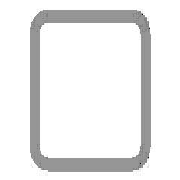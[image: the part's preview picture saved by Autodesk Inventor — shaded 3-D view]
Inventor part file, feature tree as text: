
AUTODESK INVENTOR PART (.ipt)
format: ipt  version: 2024 (Build 280153000, 153)  size: 137,728 bytes
history: native  units: mm (DEFAULTED — no unit token found)
features: other x4, plane x3, split x2, extrude x1, sketch x1
ambient origin geometry x8: Origin, YZ Plane, XZ Plane, XY Plane, X Axis, Y Axis, Z Axis, Center Point
bodies: Solid1 (feature_tree)
feature tree (11):
  parser-record x1  (decoder bookkeeping rows leaked as tree rows — omitted from the tree; the rows remain in map.json)
  other  "Driven Length"
  other  "Plano inicial"
  other  "Plano final"
  extrude  "Cuerpo"  TaperAngle=0.0deg  [1 undecoded]
  plane  "Plano de trabajo4"
  split  "Dividir1"
  plane  "Plano de trabajo5"
  split  "Dividir2"
  sketch  "Sketch3"  dims[d3=2149.2mm d4=0.0mm d10=50.8mm d11=50.8mm d12=3.175mm d13=25.4mm d14=2174.6mm d15=25.4mm d16=25.4mm d17=6.35mm d18=90.0deg d19=2149.2mm]
  plane  "Work Plane3"
note: 1 required parameter value undecoded (feature->parameter linkage not recoverable at this tier; creation-order binding heuristic only, values carry confidence <= 0.55)
